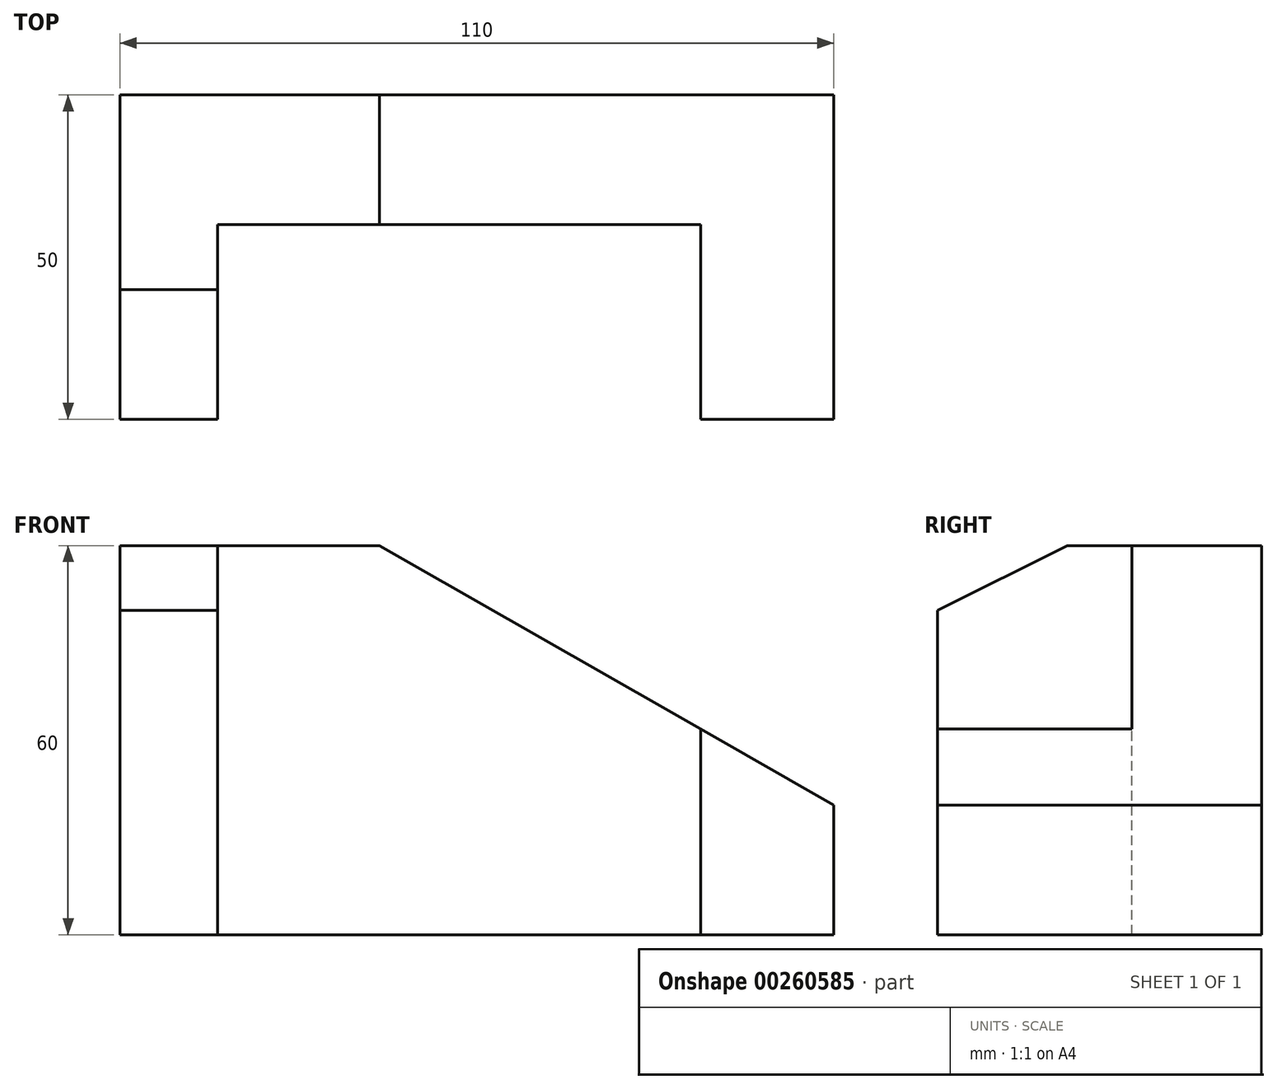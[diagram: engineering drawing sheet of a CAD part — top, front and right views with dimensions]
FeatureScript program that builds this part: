
annotation { "Feature Type Name" : "Feature", "Feature Type Description" : "" }
export const myFeature = defineFeature(function(context is Context, id is Id, definition is map)
    precondition{}
    {
        {
            var Q0;
            Q0=qCreatedBy(makeId("Front.planeOp"),FACE);
            var sketch = newSketch(context, id + "F0", { "sketchPlane" : qUnion([Q0])});
            skLineSegment(sketch, "E0.bottom", {"start": v(-49.03, 0) * mm, "end": v(60.97, 0) * mm});
            skLineSegment(sketch, "E0.top", {"start": v(-49.03, 60) * mm, "end": v(60.97, 60) * mm});
            skLineSegment(sketch, "E0.left", {"start": v(-49.03, 0) * mm, "end": v(-49.03, 60) * mm});
            skLineSegment(sketch, "E0.right", {"start": v(60.97, 0) * mm, "end": v(60.97, 60) * mm});
            skSolve(sketch);
        }
        {
            var Q0;
            Q0 = qSketchRegion(id + "F0", true);
            extrude(context, id + "F1", {"entities" : qUnion([Q0]), "depth" : 50 * mm});
        }
        {
            var Q0;
            Q0=makeQuery(id+"F1.opExtrude","CAP_FACE",FACE,{"disambiguationData":[OSD([sQuery(id+"F0.wireOp",EDGE,"E0.bottom"),sQuery(id+"F0.wireOp",EDGE,"E0.top"),sQuery(id+"F0.wireOp",EDGE,"E0.left"),sQuery(id+"F0.wireOp",EDGE,"E0.right")])],"isStart":false});
            var sketch = newSketch(context, id + "F2", { "sketchPlane" : qUnion([Q0])});
            skLineSegment(sketch, "E1.bottom", {"start": v(-34.03, 0) * mm, "end": v(40.46, 0) * mm});
            skLineSegment(sketch, "E1.top", {"start": v(-34.03, 60) * mm, "end": v(40.46, 60) * mm});
            skLineSegment(sketch, "E1.left", {"start": v(-34.03, 0) * mm, "end": v(-34.03, 60) * mm});
            skLineSegment(sketch, "E1.right", {"start": v(40.46, 0) * mm, "end": v(40.46, 60) * mm});
            skSolve(sketch);
        }
        {
            var Q0;
            Q0 = qSketchRegion(id + "F2", true);
            extrude(context, id + "F3", {"entities" : qUnion([Q0]), "operationType" : NewBodyOperationType.REMOVE, "oppositeDirection" : true, "depth" : 30 * mm});
        }
        {
            var Q0;
            Q0=makeQuery(id+"F1.opExtrude","SWEPT_FACE",FACE,{"disambiguationData":[OSD([sQuery(id+"F0.wireOp",EDGE,"E0.left")])]});
            var sketch = newSketch(context, id + "F4", { "sketchPlane" : qUnion([Q0])});
            skLineSegment(sketch, "E2", {"start": v(0, 60) * mm, "end": v(30, 60) * mm});
            skLineSegment(sketch, "E3", {"start": v(50, 0) * mm, "end": v(50, 50) * mm});
            skLineSegment(sketch, "E4", {"start": v(50, 50) * mm, "end": v(30, 60) * mm});
            skLineSegment(sketch, "E5", {"start": v(50, 60) * mm, "end": v(50, 50) * mm});
            skSolve(sketch);
        }
        {
            var Q0;
            {var subQ0=sQuery(id+"F4.wireOp",EDGE,"E4");Q0=makeQuery(id+"F4.imprint","IMPRINT",FACE,{"disambiguationData":[TD([[makeQuery(id+"F4.imprint","IMPRINT",EDGE,{"derivedFrom":subQ0}),-1.0]])]});}
            extrude(context, id + "F5", {"entities" : qUnion([Q0]), "operationType" : NewBodyOperationType.REMOVE, "oppositeDirection" : true, "depth" : 15 * mm});
        }
        {
            var Q0;
            Q0=makeQuery(id+"F1.opExtrude","CAP_FACE",FACE,{"disambiguationData":[OSD([sQuery(id+"F0.wireOp",EDGE,"E0.bottom"),sQuery(id+"F0.wireOp",EDGE,"E0.top"),sQuery(id+"F0.wireOp",EDGE,"E0.left"),sQuery(id+"F0.wireOp",EDGE,"E0.right")])],"isStart":true});
            var sketch = newSketch(context, id + "F6", { "sketchPlane" : qUnion([Q0])});
            skLineSegment(sketch, "E6", {"start": v(49.03, 60) * mm, "end": v(9.03, 60) * mm});
            skLineSegment(sketch, "E7", {"start": v(-60.97, 0) * mm, "end": v(-60.97, 20) * mm});
            skLineSegment(sketch, "E8", {"start": v(9.03, 60) * mm, "end": v(-60.97, 20) * mm});
            skLineSegment(sketch, "E9", {"start": v(-60.97, 60) * mm, "end": v(9.03, 60) * mm});
            skLineSegment(sketch, "E10", {"start": v(-60.97, 60) * mm, "end": v(-60.97, 20) * mm});
            skSolve(sketch);
        }
        {
            var Q0;
            Q0 = qSketchRegion(id + "F6", true);
            extrude(context, id + "F7", {"entities" : qUnion([Q0]), "operationType" : NewBodyOperationType.REMOVE, "oppositeDirection" : true, "depth" : 50 * mm});
        }
    });
